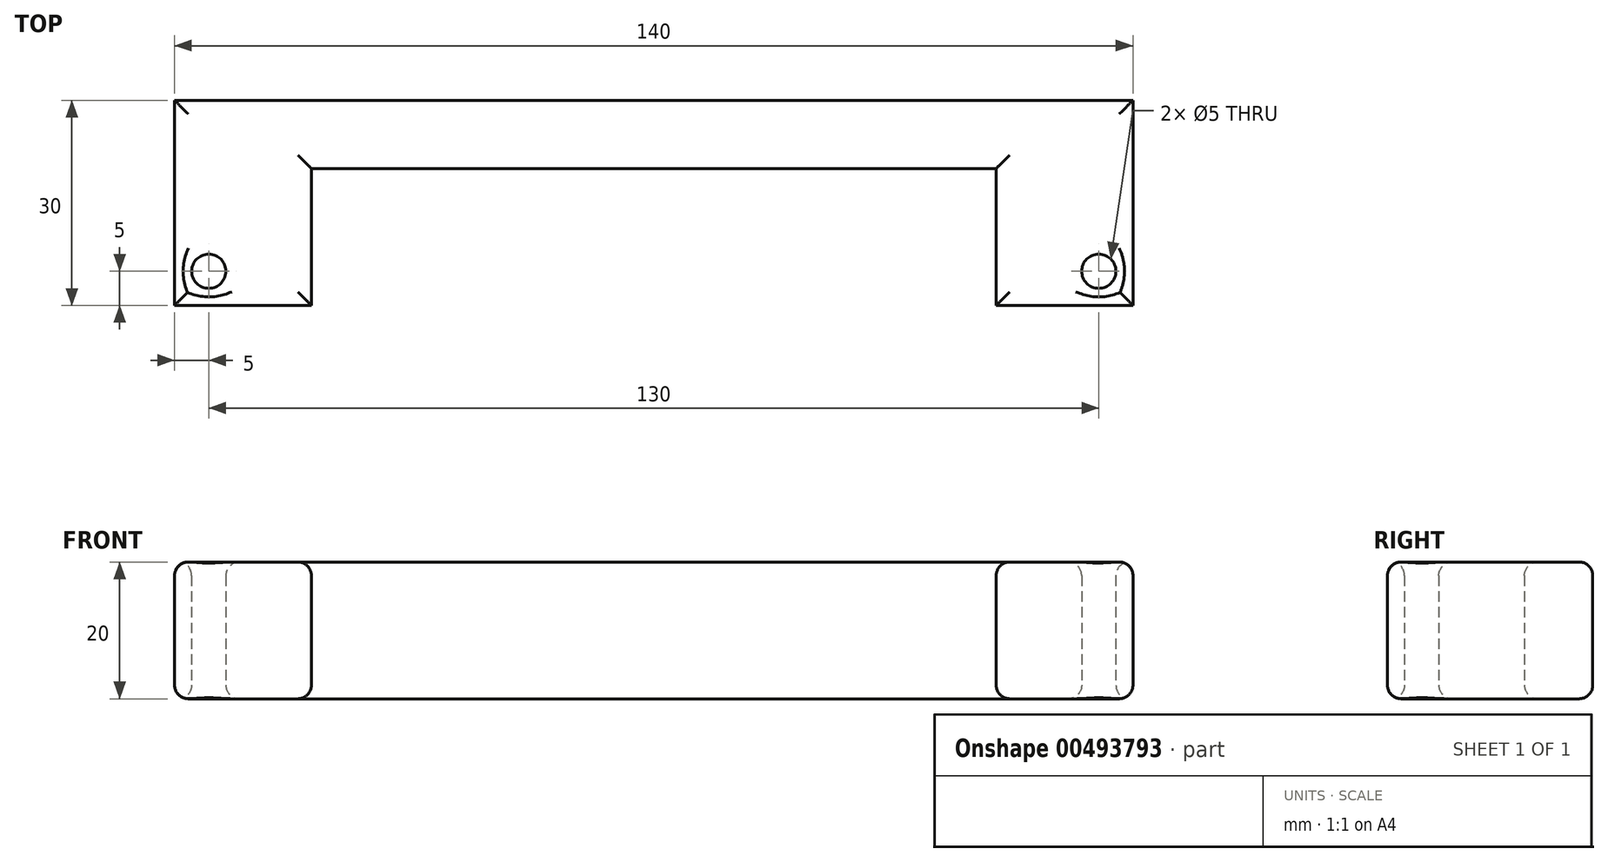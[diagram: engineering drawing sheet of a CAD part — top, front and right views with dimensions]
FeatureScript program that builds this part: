
annotation { "Feature Type Name" : "Feature", "Feature Type Description" : "" }
export const myFeature = defineFeature(function(context is Context, id is Id, definition is map)
    precondition{}
    {
        {
            var Q0;
            Q0=qCreatedBy(makeId("Top.planeOp"),FACE);
            var sketch = newSketch(context, id + "F0", { "sketchPlane" : qUnion([Q0])});
            skLineSegment(sketch, "E0", {"start": v(0, 30) * mm, "end": v(0, 20) * mm});
            skLineSegment(sketch, "E1", {"start": v(0, 20) * mm, "end": v(50, 20) * mm});
            skLineSegment(sketch, "E2", {"start": v(50, 20) * mm, "end": v(50, 0) * mm});
            skLineSegment(sketch, "E3", {"start": v(50, 0) * mm, "end": v(70, 0) * mm});
            skLineSegment(sketch, "E4", {"start": v(0, 30) * mm, "end": v(70, 30) * mm});
            skLineSegment(sketch, "E5", {"start": v(70, 30) * mm, "end": v(70, 0) * mm});
            skSolve(sketch);
        }
        {
            var Q0;
            Q0 = qSketchRegion(id + "F0", true);
            extrude(context, id + "F1", {"entities" : qUnion([Q0]), "depth" : 20 * mm});
        }
        {
            var Q0;
            Q0=qCreatedBy(makeId("Top.planeOp"),FACE);
            var sketch = newSketch(context, id + "F2", { "sketchPlane" : qUnion([Q0])});
            skPoint(sketch, "E6", {"position": v(65, 5) * mm});
            skSolve(sketch);
        }
        {
            var Q0;
            Q0=sQuery(id+"F2.wireOp",VERTEX,"E6");
            var Q1;
            Q1=makeQuery(id+"F1.opExtrude","SWEPT_BODY",BODY,{"disambiguationData":[OSD([sQuery(id+"F0.wireOp",EDGE,"E0"),sQuery(id+"F0.wireOp",EDGE,"E1"),sQuery(id+"F0.wireOp",EDGE,"E2"),sQuery(id+"F0.wireOp",EDGE,"E3"),sQuery(id+"F0.wireOp",EDGE,"E4"),sQuery(id+"F0.wireOp",EDGE,"E5")])]});
            hole(context, id + "F3", {"style" : HoleStyle.SIMPLE, "endStyle" : HoleEndStyle.THROUGH, "oppositeDirection" : true, "holeDiameter" : 5 * mm, "isTappedThrough" : true, "tappedDepth" : 12 * mm, "tapClearance" : 3, "locations" : qUnion([Q0]), "scope" : qUnion([Q1])});
        }
        {
            var Q0;
            Q0=makeQuery(id+"F1.opExtrude","SWEPT_BODY",BODY,{"disambiguationData":[OSD([sQuery(id+"F0.wireOp",EDGE,"E0"),sQuery(id+"F0.wireOp",EDGE,"E1"),sQuery(id+"F0.wireOp",EDGE,"E2"),sQuery(id+"F0.wireOp",EDGE,"E3"),sQuery(id+"F0.wireOp",EDGE,"E4"),sQuery(id+"F0.wireOp",EDGE,"E5")])]});
            var Q1;
            Q1=qCreatedBy(makeId("Right.planeOp"),FACE);
            mirror(context, id + "F4", {"operationType" : NewBodyOperationType.ADD, "entities" : qUnion([Q0]), "mirrorPlane" : qUnion([Q1])});
        }
        {
            var Q0;
            {var subQ0=makeQuery(id+"F1.opExtrude","CAP_FACE",FACE,{"disambiguationData":[OSD([sQuery(id+"F0.wireOp",EDGE,"E0"),sQuery(id+"F0.wireOp",EDGE,"E1"),sQuery(id+"F0.wireOp",EDGE,"E2"),sQuery(id+"F0.wireOp",EDGE,"E3"),sQuery(id+"F0.wireOp",EDGE,"E4"),sQuery(id+"F0.wireOp",EDGE,"E5")])],"isStart":false});Q0=makeQuery(id+"F4.boolean.opBoolean","MERGE",FACE,{"derivedFrom":[subQ0,makeQuery(id+"F4.opPattern","COPY",FACE,{"derivedFrom":subQ0,"instanceName":"1"})]});}
            var Q1;
            {var subQ0=makeQuery(id+"F1.opExtrude","CAP_FACE",FACE,{"disambiguationData":[OSD([sQuery(id+"F0.wireOp",EDGE,"E0"),sQuery(id+"F0.wireOp",EDGE,"E1"),sQuery(id+"F0.wireOp",EDGE,"E2"),sQuery(id+"F0.wireOp",EDGE,"E3"),sQuery(id+"F0.wireOp",EDGE,"E4"),sQuery(id+"F0.wireOp",EDGE,"E5")])],"isStart":true});Q1=makeQuery(id+"F4.boolean.opBoolean","MERGE",FACE,{"derivedFrom":[subQ0,makeQuery(id+"F4.opPattern","COPY",FACE,{"derivedFrom":subQ0,"instanceName":"1"})]});}
            fillet(context, id + "F5", {"entities" : qUnion([Q0, Q1]), "radius" : 2 * mm, "tangentPropagation" : true, "allowEdgeOverflow" : false});
        }
    });
